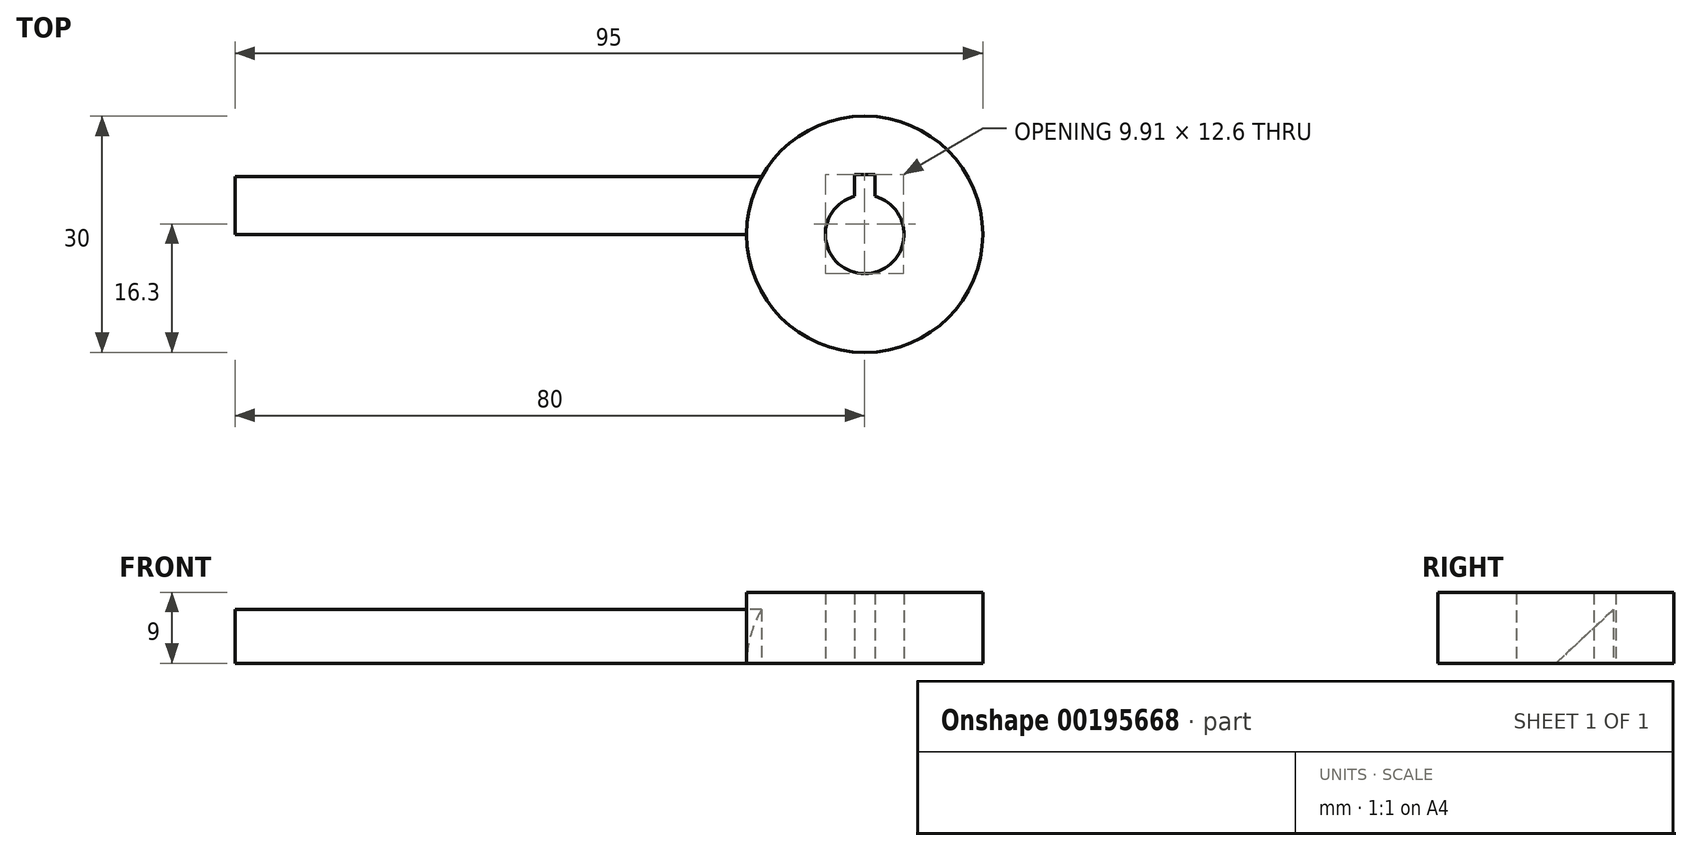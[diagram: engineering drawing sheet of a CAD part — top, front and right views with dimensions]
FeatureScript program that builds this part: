
annotation { "Feature Type Name" : "Feature", "Feature Type Description" : "" }
export const myFeature = defineFeature(function(context is Context, id is Id, definition is map)
    precondition{}
    {
        {
            var Q0;
            Q0=qCreatedBy(makeId("Top.planeOp"),FACE);
            var sketch = newSketch(context, id + "F0", { "sketchPlane" : qUnion([Q0])});
            skCircle(sketch, "E0", {"center": v(0, 0) * mm, "radius": 15 * mm});
            skCircle(sketch, "E1", {"center": v(0, 0) * mm, "radius": 5 * mm});
            skLineSegment(sketch, "E2", {"start": v(0, 7.6) * mm, "end": v(1.3, 7.6) * mm});
            skLineSegment(sketch, "E3", {"start": v(1.3, 7.6) * mm, "end": v(1.3, 4.42) * mm});
            skLineSegment(sketch, "E4", {"start": v(1.3, 4.42) * mm, "end": v(-1.3, 4.42) * mm});
            skLineSegment(sketch, "E5", {"start": v(0, 7.6) * mm, "end": v(-1.3, 7.6) * mm});
            skLineSegment(sketch, "E6", {"start": v(-1.3, 7.6) * mm, "end": v(-1.3, 4.42) * mm});
            skSolve(sketch);
        }
        {
            var Q0;
            Q0=makeQuery(id+"F0.imprint","IMPRINT",FACE,{"disambiguationData":[TD([[makeQuery(id+"F0.imprint","IMPRINT",EDGE,{"derivedFrom":sQuery(id+"F0.wireOp",EDGE,"E0")}),1.0]])]});
            extrude(context, id + "F1", {"entities" : qUnion([Q0]), "depth" : 9 * mm});
        }
        {
            var Q0;
            Q0=qCreatedBy(makeId("Right.planeOp"),FACE);
            cPlane(context, id + "F2", {"entities" : qUnion([Q0]), "cplaneType" : CPlaneType.OFFSET, "offset" : 80 * mm, "oppositeDirection" : true, "width" : 150 * mm, "height" : 150 * mm});
        }
        {
            var Q0;
            Q0=qCreatedBy(id+"F2.planeOp",FACE);
            var sketch = newSketch(context, id + "F3", { "sketchPlane" : qUnion([Q0])});
            skLineSegment(sketch, "E7", {"start": v(0, 0) * mm, "end": v(7.32, 6.82) * mm});
            skLineSegment(sketch, "E8", {"start": v(7.32, 6.82) * mm, "end": v(7.32, 0) * mm});
            skLineSegment(sketch, "E9", {"start": v(0, 0) * mm, "end": v(7.32, 0) * mm});
            skSolve(sketch);
        }
        {
            var Q0;
            Q0=makeQuery(id+"F3.imprint","IMPRINT",FACE,{"disambiguationData":[TD([[makeQuery(id+"F3.imprint","IMPRINT",EDGE,{"derivedFrom":sQuery(id+"F3.wireOp",EDGE,"E7")}),-1.0]])]});
            extrude(context, id + "F4", {"entities" : qUnion([Q0]), "operationType" : NewBodyOperationType.ADD, "depth" : 73 * mm});
        }
    });
